# Revit family: M2WU
name_source: partatom
category: Lighting Fixtures
units: mm (PartAtom-declared; Revit-internal decimal feet)

## family parameters
Cut with Voids When Loaded = No
Host = Face
Light Source = Yes
OmniClass Number = 23.80.70.14.14
OmniClass Title = Exterior Floodlights
Part Type = Normal
Room Calculation Point = No
Round Connector Dimension = Use Diameter
Shared = Yes

## types (22) — shared parameters
Apparent Load = 0 VA
Color Filter = 16777215
Default Elevation = 60"
Description = Horizontal reflector uplight
Dimming Lamp Color Temperature Shift = <None>
Finish = Die Cast Aluminium
Finish 2 = Silicon Gasket
Glass = Glass-Finish
Lamp = One
Manufacturer = Architectural Area Lighting
Model = M2WU
Tilt Angle = 90.00°
URL = https://www.currentlighting.com
Voltage = 120 V
Wattage Comments = 57 and 70 watts High Output Fluorescent

## per-type parameters (varying)
| type | Photometric Web File |
| M2WU-T2-32LED-3K-700 | M2-T2-32LED-3K-700.ies |
| M2WU-T3-32LED-3K-700 | M2-T3-32LED-3K-700.ies |
| M2WU-T4-32LED-3K-700 | M2-T4-32LED-3K-700.ies |
| M2WU-T4-32LED-3K-HSS-700 | M2-T4-32LED-3K-HSS-700.ies |
| M2WU-T5-32LED-3K-700 | M2-T5-32LED-3K-700.ies |
| M2WU-TL-32LED-3K-700 | M2-TL-32LED-3K-700.ies |
| M2WU-TR-32LED-3K-700 | M2-TR-32LED-3K-700.ies |
| M2WU-T2-32LED-4K-700 | M2-T2-32LED-4K-700.ies |
| M2WU-T3-32LED-4K-700 | M2-T3-32LED-4K-700.ies |
| M2WU-T4-32LED-4K-700 | M2-T4-32LED-4K-700.ies |
| M2WU-T4-32LED-4K-HSS-700 | M2-T4-32LED-4K-HSS-700.ies |
| M2WU-T5-32LED-4K-700 | M2-T5-32LED-4K-700.ies |
| M2WU-TL-32LED-4K-700 | M2-TL-32LED-4K-700.ies |
| M2WU-TR-32LED-4K-700 | M2-TR-32LED-4K-700.ies |
| M2WU-T2-32LED-5K-700 | M2-T2-32LED-5K-700.ies |
| M2WU-T2-32LED-5K-HSS-700 | M2-T2-32LED-5K-HSS-700.ies |
| M2WU-T3-32LED-5K-700 | M2-T3-32LED-5K-700.ies |
| M2WU-T4-32LED-5K-700 | M2-T4-32LED-5K-700.ies |
| M2WU-T4-32LED-5K-HSS-700 | M2-T4-32LED-5K-HSS-700.ies |
| M2WU-T5-32LED-5K-700 | M2-T5-32LED-5K-700.ies |
| M2WU-TL-32LED-5K-700 | M2-TL-32LED-5K-700.ies |
| M2WU-TR-32LED-5K-700 | M2-TR-32LED-5K-700.ies |

## geometry (parser evidence)
native form markers: Blend x2, Sweep x3
no freeform markers — native parametric forms only
